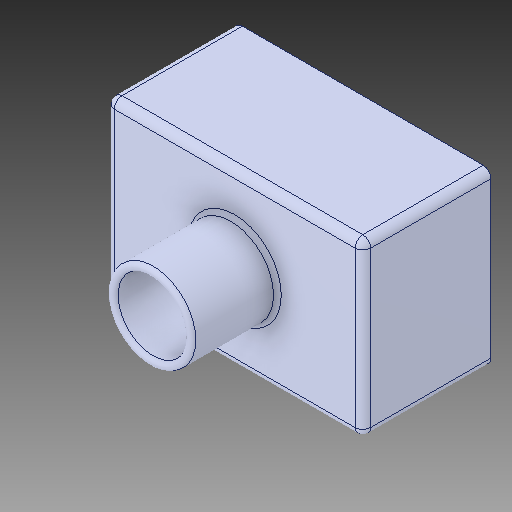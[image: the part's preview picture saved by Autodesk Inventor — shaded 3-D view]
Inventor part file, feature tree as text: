
AUTODESK INVENTOR PART (.ipt)
format: ipt  version: 2018 (Build 220112000, 112)  size: 158,720 bytes
history: native  units: in
note: dims shown in document units (in); Inventor stores cm internally (conversion verified against a paired STEP export)
features: fillet x1
ambient origin geometry x8: Origin, YZ Plane, XZ Plane, XY Plane, X Axis, Y Axis, Z Axis, Center Point
bodies: Solid1 (feature_tree)
feature tree (1):
  fillet  "Fillet10"  [1 undecoded]
note: 1 required parameter value undecoded (feature->parameter linkage not recoverable at this tier; creation-order binding heuristic only, values carry confidence <= 0.55)
